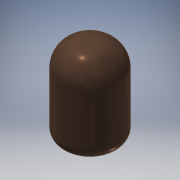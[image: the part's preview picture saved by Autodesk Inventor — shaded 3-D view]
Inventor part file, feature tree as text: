
AUTODESK INVENTOR PART (.ipt)
format: ipt  version: 2016 (Build 200138000, 138)  size: 130,048 bytes
history: native  units: in
note: dims shown in document units (in); Inventor stores cm internally (conversion verified against a paired STEP export)
features: fillet x2, extrude x1, sketch x1
ambient origin geometry x8: Origin, YZ Plane, XZ Plane, XY Plane, X Axis, Y Axis, Z Axis, Center Point
bodies: Solid1 (feature_tree)
feature tree (4):
  extrude  "Extrusion1"  Depth=36.0in TaperAngle=0.0deg
  fillet  "Fillet1"  Radius=10.0in
  fillet  "Fillet2"  Radius=5.0in
  sketch  "Sketch1"  dims[d0=24.0in d1=36.0in d2=0.0in d3=10.0in d4=5.0in]
